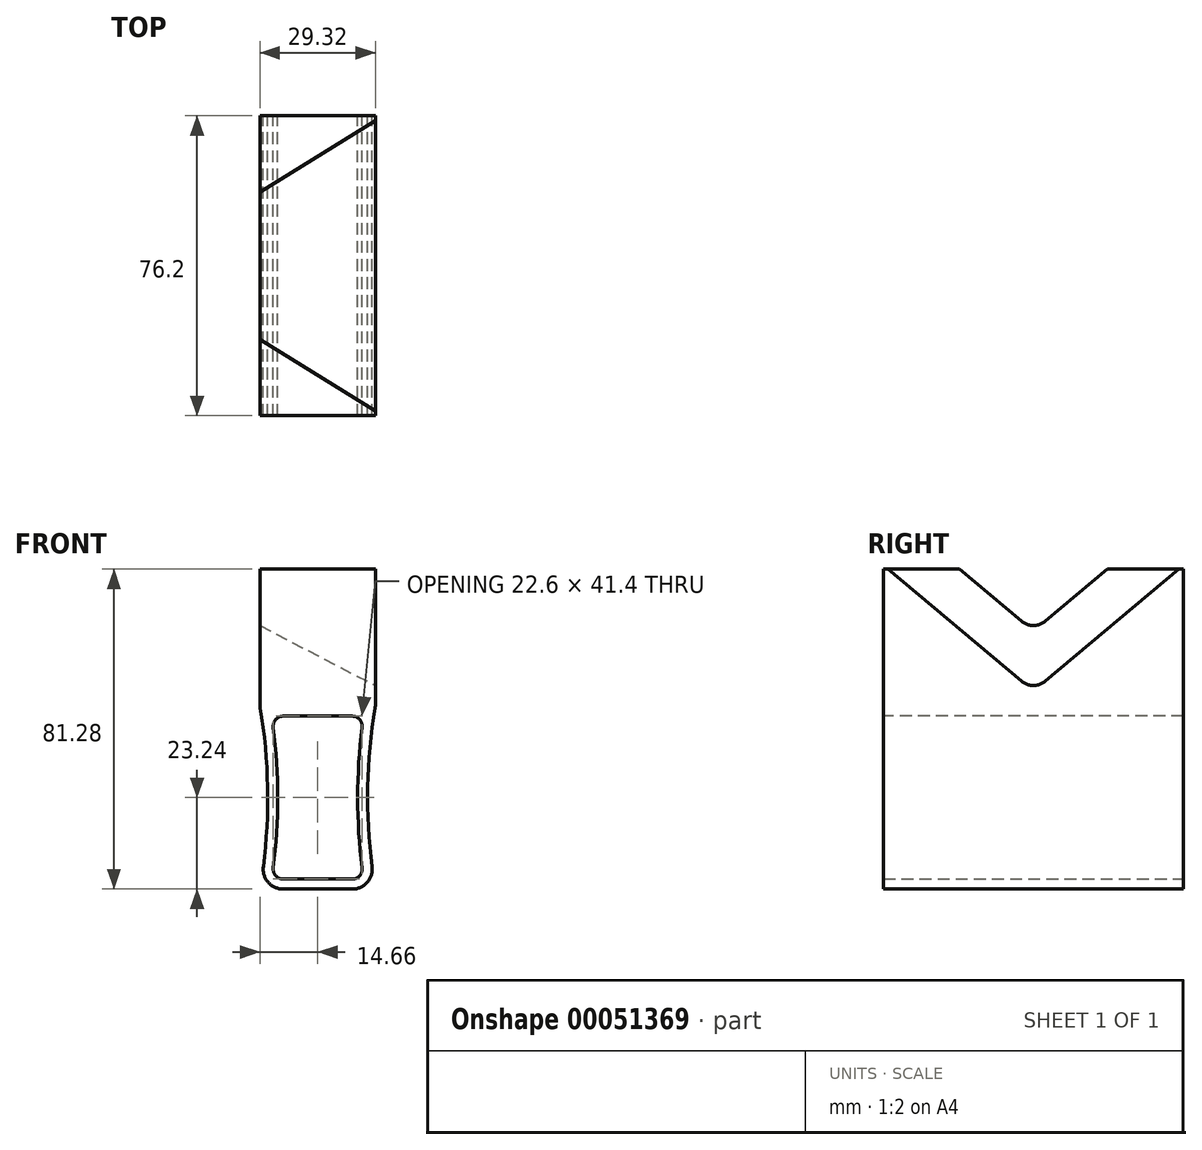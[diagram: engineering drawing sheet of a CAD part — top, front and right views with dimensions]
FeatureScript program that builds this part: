
annotation { "Feature Type Name" : "Feature", "Feature Type Description" : "" }
export const myFeature = defineFeature(function(context is Context, id is Id, definition is map)
    precondition{}
    {
        {
            var Q0;
            Q0=qCreatedBy(makeId("Front.planeOp"),FACE);
            var sketch = newSketch(context, id + "F0", { "sketchPlane" : qUnion([Q0])});
            skLineSegment(sketch, "E0.bottom", {"start": v(-12.95, 20.7) * mm, "end": v(10.41, 20.7) * mm});
            skLineSegment(sketch, "E0.top", {"start": v(-12.95, -20.7) * mm, "end": v(10.41, -20.7) * mm});
            skLineSegment(sketch, "E1.bottom", {"start": v(-15.93, 58.04) * mm, "end": v(13.39, 58.04) * mm});
            skLineSegment(sketch, "E1.top", {"start": v(-15.93, -23.24) * mm, "end": v(13.39, -23.24) * mm});
            skArc(sketch, "E2", {"start": v(-12.95, -20.7) * mm, "mid": v(-11.43, 0) * mm, "end": v(-12.95, 20.7) * mm});
            skArc(sketch, "E3", {"start": v(10.41, 20.7) * mm, "mid": v(8.9, 0) * mm, "end": v(10.41, -20.7) * mm});
            skArc(sketch, "E4.0", {"start": v(-15.93, -23.24) * mm, "mid": v(-13.97, 0) * mm, "end": v(-15.93, 23.24) * mm});
            skLineSegment(sketch, "E5", {"start": v(-15.93, 23.24) * mm, "end": v(-15.93, 58.04) * mm});
            skArc(sketch, "E6.0", {"start": v(13.39, 23.24) * mm, "mid": v(11.43, 0) * mm, "end": v(13.39, -23.24) * mm});
            skLineSegment(sketch, "E7", {"start": v(13.39, 23.24) * mm, "end": v(13.39, 58.04) * mm});
            skSolve(sketch);
        }
        {
            var Q0;
            Q0 = qSketchRegion(id + "F0", true);
            extrude(context, id + "F1", {"entities" : qUnion([Q0]), "endBound" : BoundingType.SYMMETRIC, "depth" : 76.2 * mm});
        }
        {
            var Q0;
            Q0=makeQuery(id+"F1.opExtrude","SWEPT_FACE",FACE,{"disambiguationData":[OSD([sQuery(id+"F0.wireOp",EDGE,"E7")])]});
            var sketch = newSketch(context, id + "F2", { "sketchPlane" : qUnion([Q0])});
            skLineSegment(sketch, "E8", {"start": v(-36.93, 58.04) * mm, "end": v(0, 27.05) * mm});
            skLineSegment(sketch, "E9", {"start": v(0, 27.05) * mm, "end": v(36.93, 58.04) * mm});
            skLineSegment(sketch, "E10", {"start": v(36.93, 58.04) * mm, "end": v(-36.93, 58.04) * mm});
            skSolve(sketch);
        }
        {
            var Q0;
            Q0=qCreatedBy(makeId("Front.planeOp"),FACE);
            var sketch = newSketch(context, id + "F3", { "sketchPlane" : qUnion([Q0])});
            skLineSegment(sketch, "E11", {"start": v(13.39, 27.05) * mm, "end": v(-15.93, 42.3) * mm});
            skSolve(sketch);
        }
        {
            var Q0;
            Q0 = qSketchRegion(id + "F2", true);
            var Q1;
            Q1 = qConstructionFilter(qBodyType(qCreatedBy(id + "F3" ,EDGE), BodyType.WIRE), ConstructionObject.NO);
            var Q2;
            Q2 = qConstructionFilter(qBodyType(qCreatedBy(id + "F3" ,EDGE), BodyType.WIRE), ConstructionObject.NO);
            sweep(context, id + "F4", {"operationType" : NewBodyOperationType.REMOVE, "profiles" : qUnion([Q0]), "path" : qUnion([Q1, Q2])});
        }
        {
            var Q0;
            Q0=makeQuery(id+"F1.opExtrude","SWEPT_EDGE",EDGE,{"disambiguationData":[OSD([sQuery(id+"F0.wireOp",EDGE,"E0.top"),sQuery(id+"F0.wireOp",EDGE,"E2")])]});
            var Q1;
            Q1=makeQuery(id+"F1.opExtrude","SWEPT_EDGE",EDGE,{"disambiguationData":[OSD([sQuery(id+"F0.wireOp",EDGE,"E0.top"),sQuery(id+"F0.wireOp",EDGE,"E3")])]});
            var Q2;
            Q2=makeQuery(id+"F1.opExtrude","SWEPT_EDGE",EDGE,{"disambiguationData":[OSD([sQuery(id+"F0.wireOp",EDGE,"E0.bottom"),sQuery(id+"F0.wireOp",EDGE,"E3")])]});
            var Q3;
            Q3=makeQuery(id+"F1.opExtrude","SWEPT_EDGE",EDGE,{"disambiguationData":[OSD([sQuery(id+"F0.wireOp",EDGE,"E0.bottom"),sQuery(id+"F0.wireOp",EDGE,"E2")])]});
            fillet(context, id + "F5", {"entities" : qUnion([Q0, Q1, Q2, Q3]), "radius" : 2.54 * mm, "tangentPropagation" : true, "allowEdgeOverflow" : false});
        }
        {
            var Q0;
            Q0=makeQuery(id+"F1.opExtrude","SWEPT_EDGE",EDGE,{"disambiguationData":[OSD([sQuery(id+"F0.wireOp",EDGE,"E1.top"),sQuery(id+"F0.wireOp",EDGE,"E6.0")])]});
            var Q1;
            Q1=makeQuery(id+"F1.opExtrude","SWEPT_EDGE",EDGE,{"disambiguationData":[OSD([sQuery(id+"F0.wireOp",EDGE,"E1.top"),sQuery(id+"F0.wireOp",EDGE,"E4.0")])]});
            var Q2;
            Q2=makeQuery(id+"F1.opExtrude","SWEPT_EDGE",EDGE,{"disambiguationData":[OSD([sQuery(id+"F0.wireOp",EDGE,"E4.0"),sQuery(id+"F0.wireOp",EDGE,"E5")])]});
            var Q3;
            Q3=makeQuery(id+"F1.opExtrude","SWEPT_EDGE",EDGE,{"disambiguationData":[OSD([sQuery(id+"F0.wireOp",EDGE,"E6.0"),sQuery(id+"F0.wireOp",EDGE,"E7")])]});
            var Q4;
            Q4=makeQuery(id+"F4.boolean.opBoolean","COPY",EDGE,{"derivedFrom":makeQuery(id+"F4.opSweep","SWEPT_EDGE",EDGE,{"disambiguationData":[OSD([sQuery(id+"F2.wireOp",EDGE,"E8"),sQuery(id+"F2.wireOp",EDGE,"E9"),sQuery(id+"F3.wireOp",EDGE,"E11")])]})});
            fillet(context, id + "F6", {"entities" : qUnion([Q0, Q1, Q2, Q3, Q4]), "radius" : 5.08 * mm, "tangentPropagation" : true, "allowEdgeOverflow" : false});
        }
    });
